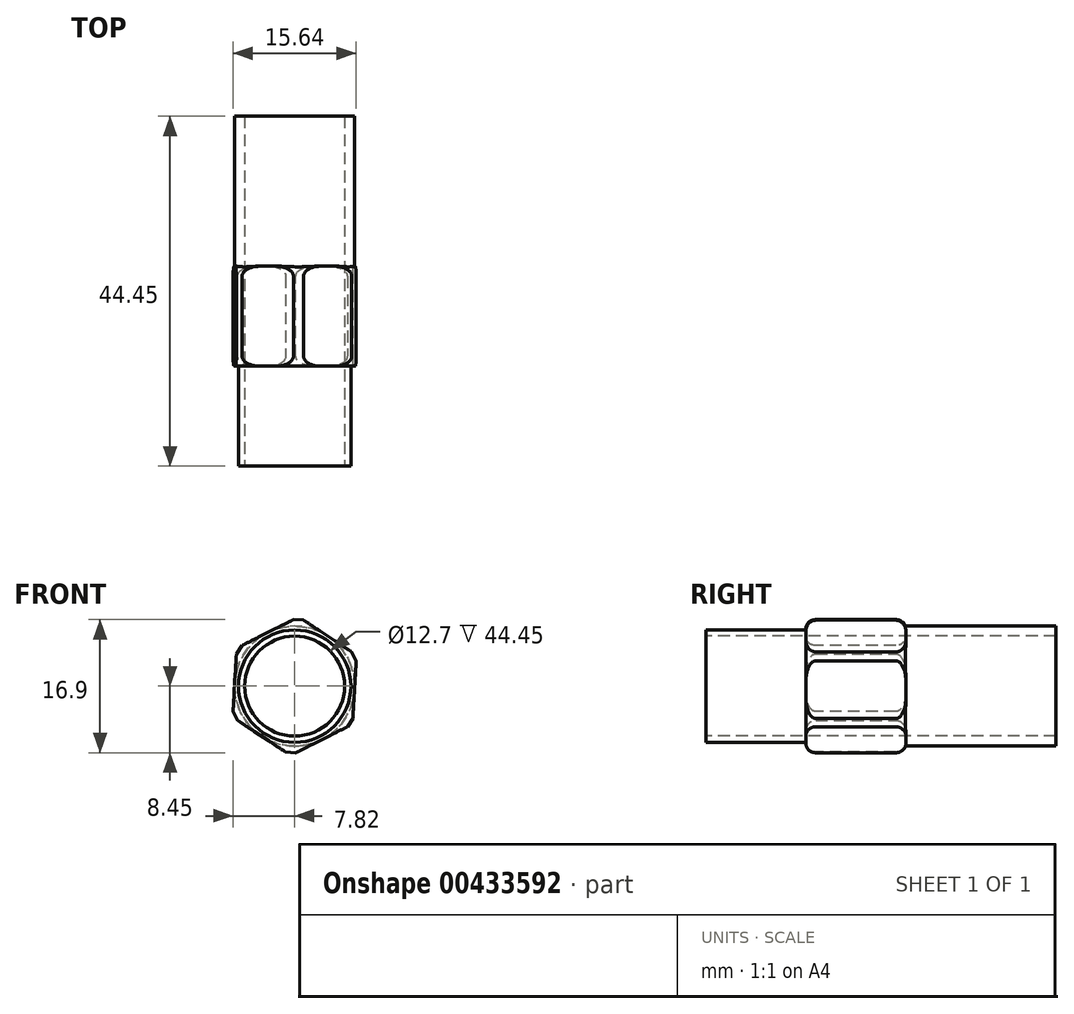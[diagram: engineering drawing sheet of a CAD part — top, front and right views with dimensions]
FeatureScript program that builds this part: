
annotation { "Feature Type Name" : "Feature", "Feature Type Description" : "" }
export const myFeature = defineFeature(function(context is Context, id is Id, definition is map)
    precondition{}
    {
        {
            var Q0;
            Q0=qCreatedBy(makeId("Front.planeOp"),FACE);
            var sketch = newSketch(context, id + "F0", { "sketchPlane" : qUnion([Q0])});
            skCircle(sketch, "E0", {"center": v(0, 0) * mm, "radius": 7.62 * mm});
            skSolve(sketch);
        }
        {
            var Q0;
            Q0=makeQuery(id+"F0.imprint","IMPRINT",FACE,{"disambiguationData":[TD([[makeQuery(id+"F0.imprint","IMPRINT",EDGE,{"derivedFrom":sQuery(id+"F0.wireOp",EDGE,"E0")}),1.0]])]});
            extrude(context, id + "F1", {"entities" : qUnion([Q0]), "depth" : 19.05 * mm});
        }
        {
            var Q0;
            Q0=makeQuery(id+"F1.opExtrude","CAP_FACE",FACE,{"disambiguationData":[OSD([sQuery(id+"F0.wireOp",EDGE,"E0")])],"isStart":false});
            var sketch = newSketch(context, id + "F2", { "sketchPlane" : qUnion([Q0])});
            skCircle(sketch, "E1.cCircle", {"center": v(0, 0) * mm, "radius": 7.62 * mm, "construction": true});
            skLineSegment(sketch, "E1.0", {"start": v(-7.35, 4.84) * mm, "end": v(0.51, 8.78) * mm});
            skLineSegment(sketch, "E1.1", {"start": v(0.51, 8.78) * mm, "end": v(7.86, 3.95) * mm});
            skLineSegment(sketch, "E1.2", {"start": v(7.86, 3.95) * mm, "end": v(7.35, -4.84) * mm});
            skLineSegment(sketch, "E1.3", {"start": v(7.35, -4.84) * mm, "end": v(-0.51, -8.78) * mm});
            skLineSegment(sketch, "E1.4", {"start": v(-0.51, -8.78) * mm, "end": v(-7.86, -3.95) * mm});
            skLineSegment(sketch, "E1.5", {"start": v(-7.86, -3.95) * mm, "end": v(-7.35, 4.84) * mm});
            skPoint(sketch, "E1.0.midPoint", {"position": v(-3.42, 6.8) * mm});
            skSolve(sketch);
        }
        {
            var Q0;
            {var subQ0=sQuery(id+"F2.wireOp",EDGE,"E1.2");var subQ1=sQuery(id+"F2.wireOp",EDGE,"E1.1");var subQ2=makeQuery(id+"F2.imprint","INTERSECT",VERTEX,{"derivedFrom":[subQ1,subQ0]});Q0=makeQuery(id+"F2.imprint","IMPRINT",FACE,{"disambiguationData":[TD([[makeQuery(id+"F2.imprint","IMPRINT",EDGE,{"disambiguationData":[TD([[subQ2,1.0]])],"derivedFrom":subQ1}),-1.0]])]});}
            var Q1;
            {var subQ0=makeQuery(id+"F1.opExtrude","CAP_EDGE",EDGE,{"disambiguationData":[OSD([sQuery(id+"F0.wireOp",EDGE,"E0")])],"isStart":false});var subQ4=makeQuery(id+"F2.imprint","INTERSECT",VERTEX,{"derivedFrom":[subQ0,sQuery(id+"F2.wireOp",EDGE,"E1.0")]});Q1=makeQuery(id+"F2.imprint","IMPRINT",FACE,{"disambiguationData":[TD([[makeQuery(id+"F2.imprint","IMPRINT",EDGE,{"disambiguationData":[TD([[subQ4,1.0]])],"derivedFrom":subQ0}),1.0]])]});}
            var Q2;
            {var subQ0=sQuery(id+"F2.wireOp",EDGE,"E1.3");var subQ1=sQuery(id+"F2.wireOp",EDGE,"E1.2");var subQ2=makeQuery(id+"F2.imprint","INTERSECT",VERTEX,{"derivedFrom":[subQ1,subQ0]});Q2=makeQuery(id+"F2.imprint","IMPRINT",FACE,{"disambiguationData":[TD([[makeQuery(id+"F2.imprint","IMPRINT",EDGE,{"disambiguationData":[TD([[subQ2,1.0]])],"derivedFrom":subQ1}),-1.0]])]});}
            var Q3;
            {var subQ0=sQuery(id+"F2.wireOp",EDGE,"E1.4");var subQ1=sQuery(id+"F2.wireOp",EDGE,"E1.3");var subQ2=makeQuery(id+"F2.imprint","INTERSECT",VERTEX,{"derivedFrom":[subQ1,subQ0]});Q3=makeQuery(id+"F2.imprint","IMPRINT",FACE,{"disambiguationData":[TD([[makeQuery(id+"F2.imprint","IMPRINT",EDGE,{"disambiguationData":[TD([[subQ2,1.0]])],"derivedFrom":subQ1}),-1.0]])]});}
            var Q4;
            {var subQ0=sQuery(id+"F2.wireOp",EDGE,"E1.5");var subQ1=sQuery(id+"F2.wireOp",EDGE,"E1.4");var subQ2=makeQuery(id+"F2.imprint","INTERSECT",VERTEX,{"derivedFrom":[subQ1,subQ0]});Q4=makeQuery(id+"F2.imprint","IMPRINT",FACE,{"disambiguationData":[TD([[makeQuery(id+"F2.imprint","IMPRINT",EDGE,{"disambiguationData":[TD([[subQ2,1.0]])],"derivedFrom":subQ1}),-1.0]])]});}
            var Q5;
            {var subQ0=sQuery(id+"F2.wireOp",EDGE,"E1.5");var subQ1=sQuery(id+"F2.wireOp",EDGE,"E1.0");var subQ2=makeQuery(id+"F2.imprint","INTERSECT",VERTEX,{"derivedFrom":[subQ1,subQ0]});Q5=makeQuery(id+"F2.imprint","IMPRINT",FACE,{"disambiguationData":[TD([[makeQuery(id+"F2.imprint","IMPRINT",EDGE,{"disambiguationData":[TD([[subQ2,-1.0]])],"derivedFrom":subQ1}),-1.0]])]});}
            var Q6;
            {var subQ0=sQuery(id+"F2.wireOp",EDGE,"E1.1");var subQ1=sQuery(id+"F2.wireOp",EDGE,"E1.0");var subQ2=makeQuery(id+"F2.imprint","INTERSECT",VERTEX,{"derivedFrom":[subQ1,subQ0]});Q6=makeQuery(id+"F2.imprint","IMPRINT",FACE,{"disambiguationData":[TD([[makeQuery(id+"F2.imprint","IMPRINT",EDGE,{"disambiguationData":[TD([[subQ2,1.0]])],"derivedFrom":subQ1}),-1.0]])]});}
            extrude(context, id + "F3", {"entities" : qUnion([Q0, Q1, Q2, Q3, Q4, Q5, Q6]), "operationType" : NewBodyOperationType.ADD, "depth" : 12.7 * mm});
        }
        {
            var Q0;
            Q0=makeQuery(id+"F3.opExtrude","SWEPT_EDGE",EDGE,{"disambiguationData":[OSD([sQuery(id+"F2.wireOp",EDGE,"E1.1"),sQuery(id+"F2.wireOp",EDGE,"E1.2")])]});
            var Q1;
            Q1=makeQuery(id+"F3.opExtrude","SWEPT_EDGE",EDGE,{"disambiguationData":[OSD([sQuery(id+"F2.wireOp",EDGE,"E1.2"),sQuery(id+"F2.wireOp",EDGE,"E1.3")])]});
            var Q2;
            Q2=makeQuery(id+"F3.opExtrude","SWEPT_EDGE",EDGE,{"disambiguationData":[OSD([sQuery(id+"F2.wireOp",EDGE,"E1.3"),sQuery(id+"F2.wireOp",EDGE,"E1.4")])]});
            var Q3;
            Q3=makeQuery(id+"F3.opExtrude","SWEPT_EDGE",EDGE,{"disambiguationData":[OSD([sQuery(id+"F2.wireOp",EDGE,"E1.4"),sQuery(id+"F2.wireOp",EDGE,"E1.5")])]});
            var Q4;
            Q4=makeQuery(id+"F3.opExtrude","SWEPT_EDGE",EDGE,{"disambiguationData":[OSD([sQuery(id+"F2.wireOp",EDGE,"E1.0"),sQuery(id+"F2.wireOp",EDGE,"E1.5")])]});
            var Q5;
            Q5=makeQuery(id+"F3.opExtrude","SWEPT_EDGE",EDGE,{"disambiguationData":[OSD([sQuery(id+"F2.wireOp",EDGE,"E1.0"),sQuery(id+"F2.wireOp",EDGE,"E1.1")])]});
            chamfer(context, id + "F4", {"entities" : qUnion([Q0, Q1, Q2, Q3, Q4, Q5]), "width" : 1.27 * mm, "tangentPropagation" : true});
        }
        {
            var Q0;
            {var subQ0=sQuery(id+"F2.wireOp",EDGE,"E1.0");var subQ1=sQuery(id+"F2.wireOp",EDGE,"E1.1");var subQ2=makeQuery(id+"F3.opExtrude","CAP_FACE",FACE,{"disambiguationData":[OSD([subQ0,subQ1,sQuery(id+"F2.wireOp",EDGE,"E1.2"),sQuery(id+"F2.wireOp",EDGE,"E1.3"),sQuery(id+"F2.wireOp",EDGE,"E1.4"),sQuery(id+"F2.wireOp",EDGE,"E1.5")])],"isStart":true});Q0=makeQuery(id+"F4.opChamfer","BLEND_EDGE",EDGE,{"blendedFrom":[makeQuery(id+"F3.opExtrude","SWEPT_EDGE",EDGE,{"disambiguationData":[OSD([subQ0,subQ1])]}),makeQuery(id+"F3.boolean.opBoolean","SPLIT",FACE,{"disambiguationData":[TD([makeQuery(id+"F1.opExtrude","SWEPT_FACE",FACE,{"disambiguationData":[OSD([sQuery(id+"F0.wireOp",EDGE,"E0")])]}),makeQuery(id+"F3.opExtrude","SWEPT_FACE",FACE,{"disambiguationData":[OSD([subQ0])]}),subQ2,makeQuery(id+"F3.opExtrude","SWEPT_FACE",FACE,{"disambiguationData":[OSD([subQ1])]})])],"derivedFrom":subQ2})],"blendedInto":[makeQuery(id+"F3.boolean.opBoolean","SPLIT",FACE,{"disambiguationData":[TD([makeQuery(id+"F1.opExtrude","SWEPT_FACE",FACE,{"disambiguationData":[OSD([sQuery(id+"F0.wireOp",EDGE,"E0")])]}),makeQuery(id+"F3.opExtrude","SWEPT_FACE",FACE,{"disambiguationData":[OSD([subQ0])]}),subQ2,makeQuery(id+"F3.opExtrude","SWEPT_FACE",FACE,{"disambiguationData":[OSD([subQ1])]})])],"derivedFrom":subQ2})]});}
            var Q1;
            {var subQ0=sQuery(id+"F2.wireOp",EDGE,"E1.5");var subQ1=sQuery(id+"F2.wireOp",EDGE,"E1.0");var subQ2=makeQuery(id+"F3.opExtrude","CAP_FACE",FACE,{"disambiguationData":[OSD([subQ1,sQuery(id+"F2.wireOp",EDGE,"E1.1"),sQuery(id+"F2.wireOp",EDGE,"E1.2"),sQuery(id+"F2.wireOp",EDGE,"E1.3"),sQuery(id+"F2.wireOp",EDGE,"E1.4"),subQ0])],"isStart":true});Q1=makeQuery(id+"F4.opChamfer","BLEND_EDGE",EDGE,{"blendedFrom":[makeQuery(id+"F3.opExtrude","SWEPT_EDGE",EDGE,{"disambiguationData":[OSD([subQ1,subQ0])]}),makeQuery(id+"F3.boolean.opBoolean","SPLIT",FACE,{"disambiguationData":[TD([makeQuery(id+"F1.opExtrude","SWEPT_FACE",FACE,{"disambiguationData":[OSD([sQuery(id+"F0.wireOp",EDGE,"E0")])]}),makeQuery(id+"F3.opExtrude","SWEPT_FACE",FACE,{"disambiguationData":[OSD([subQ1])]}),subQ2,makeQuery(id+"F3.opExtrude","SWEPT_FACE",FACE,{"disambiguationData":[OSD([subQ0])]})])],"derivedFrom":subQ2})],"blendedInto":[makeQuery(id+"F3.boolean.opBoolean","SPLIT",FACE,{"disambiguationData":[TD([makeQuery(id+"F1.opExtrude","SWEPT_FACE",FACE,{"disambiguationData":[OSD([sQuery(id+"F0.wireOp",EDGE,"E0")])]}),makeQuery(id+"F3.opExtrude","SWEPT_FACE",FACE,{"disambiguationData":[OSD([subQ1])]}),subQ2,makeQuery(id+"F3.opExtrude","SWEPT_FACE",FACE,{"disambiguationData":[OSD([subQ0])]})])],"derivedFrom":subQ2})]});}
            var Q2;
            {var subQ0=sQuery(id+"F2.wireOp",EDGE,"E1.5");var subQ1=sQuery(id+"F2.wireOp",EDGE,"E1.4");var subQ2=makeQuery(id+"F3.opExtrude","CAP_FACE",FACE,{"disambiguationData":[OSD([sQuery(id+"F2.wireOp",EDGE,"E1.0"),sQuery(id+"F2.wireOp",EDGE,"E1.1"),sQuery(id+"F2.wireOp",EDGE,"E1.2"),sQuery(id+"F2.wireOp",EDGE,"E1.3"),subQ1,subQ0])],"isStart":true});Q2=makeQuery(id+"F4.opChamfer","BLEND_EDGE",EDGE,{"blendedFrom":[makeQuery(id+"F3.opExtrude","SWEPT_EDGE",EDGE,{"disambiguationData":[OSD([subQ1,subQ0])]}),makeQuery(id+"F3.boolean.opBoolean","SPLIT",FACE,{"disambiguationData":[TD([makeQuery(id+"F1.opExtrude","SWEPT_FACE",FACE,{"disambiguationData":[OSD([sQuery(id+"F0.wireOp",EDGE,"E0")])]}),subQ2,makeQuery(id+"F3.opExtrude","SWEPT_FACE",FACE,{"disambiguationData":[OSD([subQ1])]}),makeQuery(id+"F3.opExtrude","SWEPT_FACE",FACE,{"disambiguationData":[OSD([subQ0])]})])],"derivedFrom":subQ2})],"blendedInto":[makeQuery(id+"F3.boolean.opBoolean","SPLIT",FACE,{"disambiguationData":[TD([makeQuery(id+"F1.opExtrude","SWEPT_FACE",FACE,{"disambiguationData":[OSD([sQuery(id+"F0.wireOp",EDGE,"E0")])]}),subQ2,makeQuery(id+"F3.opExtrude","SWEPT_FACE",FACE,{"disambiguationData":[OSD([subQ1])]}),makeQuery(id+"F3.opExtrude","SWEPT_FACE",FACE,{"disambiguationData":[OSD([subQ0])]})])],"derivedFrom":subQ2})]});}
            var Q3;
            {var subQ0=sQuery(id+"F2.wireOp",EDGE,"E1.4");var subQ1=sQuery(id+"F2.wireOp",EDGE,"E1.3");var subQ2=makeQuery(id+"F3.opExtrude","CAP_FACE",FACE,{"disambiguationData":[OSD([sQuery(id+"F2.wireOp",EDGE,"E1.0"),sQuery(id+"F2.wireOp",EDGE,"E1.1"),sQuery(id+"F2.wireOp",EDGE,"E1.2"),subQ1,subQ0,sQuery(id+"F2.wireOp",EDGE,"E1.5")])],"isStart":true});Q3=makeQuery(id+"F4.opChamfer","BLEND_EDGE",EDGE,{"blendedFrom":[makeQuery(id+"F3.opExtrude","SWEPT_EDGE",EDGE,{"disambiguationData":[OSD([subQ1,subQ0])]}),makeQuery(id+"F3.boolean.opBoolean","SPLIT",FACE,{"disambiguationData":[TD([makeQuery(id+"F1.opExtrude","SWEPT_FACE",FACE,{"disambiguationData":[OSD([sQuery(id+"F0.wireOp",EDGE,"E0")])]}),subQ2,makeQuery(id+"F3.opExtrude","SWEPT_FACE",FACE,{"disambiguationData":[OSD([subQ1])]}),makeQuery(id+"F3.opExtrude","SWEPT_FACE",FACE,{"disambiguationData":[OSD([subQ0])]})])],"derivedFrom":subQ2})],"blendedInto":[makeQuery(id+"F3.boolean.opBoolean","SPLIT",FACE,{"disambiguationData":[TD([makeQuery(id+"F1.opExtrude","SWEPT_FACE",FACE,{"disambiguationData":[OSD([sQuery(id+"F0.wireOp",EDGE,"E0")])]}),subQ2,makeQuery(id+"F3.opExtrude","SWEPT_FACE",FACE,{"disambiguationData":[OSD([subQ1])]}),makeQuery(id+"F3.opExtrude","SWEPT_FACE",FACE,{"disambiguationData":[OSD([subQ0])]})])],"derivedFrom":subQ2})]});}
            var Q4;
            {var subQ0=sQuery(id+"F2.wireOp",EDGE,"E1.3");var subQ1=sQuery(id+"F2.wireOp",EDGE,"E1.2");var subQ2=makeQuery(id+"F3.opExtrude","CAP_FACE",FACE,{"disambiguationData":[OSD([sQuery(id+"F2.wireOp",EDGE,"E1.0"),sQuery(id+"F2.wireOp",EDGE,"E1.1"),subQ1,subQ0,sQuery(id+"F2.wireOp",EDGE,"E1.4"),sQuery(id+"F2.wireOp",EDGE,"E1.5")])],"isStart":true});Q4=makeQuery(id+"F4.opChamfer","BLEND_EDGE",EDGE,{"blendedFrom":[makeQuery(id+"F3.opExtrude","SWEPT_EDGE",EDGE,{"disambiguationData":[OSD([subQ1,subQ0])]}),makeQuery(id+"F3.boolean.opBoolean","SPLIT",FACE,{"disambiguationData":[TD([makeQuery(id+"F1.opExtrude","SWEPT_FACE",FACE,{"disambiguationData":[OSD([sQuery(id+"F0.wireOp",EDGE,"E0")])]}),subQ2,makeQuery(id+"F3.opExtrude","SWEPT_FACE",FACE,{"disambiguationData":[OSD([subQ1])]}),makeQuery(id+"F3.opExtrude","SWEPT_FACE",FACE,{"disambiguationData":[OSD([subQ0])]})])],"derivedFrom":subQ2})],"blendedInto":[makeQuery(id+"F3.boolean.opBoolean","SPLIT",FACE,{"disambiguationData":[TD([makeQuery(id+"F1.opExtrude","SWEPT_FACE",FACE,{"disambiguationData":[OSD([sQuery(id+"F0.wireOp",EDGE,"E0")])]}),subQ2,makeQuery(id+"F3.opExtrude","SWEPT_FACE",FACE,{"disambiguationData":[OSD([subQ1])]}),makeQuery(id+"F3.opExtrude","SWEPT_FACE",FACE,{"disambiguationData":[OSD([subQ0])]})])],"derivedFrom":subQ2})]});}
            var Q5;
            {var subQ0=sQuery(id+"F2.wireOp",EDGE,"E1.2");var subQ1=sQuery(id+"F2.wireOp",EDGE,"E1.1");var subQ2=makeQuery(id+"F3.opExtrude","CAP_FACE",FACE,{"disambiguationData":[OSD([sQuery(id+"F2.wireOp",EDGE,"E1.0"),subQ1,subQ0,sQuery(id+"F2.wireOp",EDGE,"E1.3"),sQuery(id+"F2.wireOp",EDGE,"E1.4"),sQuery(id+"F2.wireOp",EDGE,"E1.5")])],"isStart":true});Q5=makeQuery(id+"F4.opChamfer","BLEND_EDGE",EDGE,{"blendedFrom":[makeQuery(id+"F3.opExtrude","SWEPT_EDGE",EDGE,{"disambiguationData":[OSD([subQ1,subQ0])]}),makeQuery(id+"F3.boolean.opBoolean","SPLIT",FACE,{"disambiguationData":[TD([makeQuery(id+"F1.opExtrude","SWEPT_FACE",FACE,{"disambiguationData":[OSD([sQuery(id+"F0.wireOp",EDGE,"E0")])]}),subQ2,makeQuery(id+"F3.opExtrude","SWEPT_FACE",FACE,{"disambiguationData":[OSD([subQ1])]}),makeQuery(id+"F3.opExtrude","SWEPT_FACE",FACE,{"disambiguationData":[OSD([subQ0])]})])],"derivedFrom":subQ2})],"blendedInto":[makeQuery(id+"F3.boolean.opBoolean","SPLIT",FACE,{"disambiguationData":[TD([makeQuery(id+"F1.opExtrude","SWEPT_FACE",FACE,{"disambiguationData":[OSD([sQuery(id+"F0.wireOp",EDGE,"E0")])]}),subQ2,makeQuery(id+"F3.opExtrude","SWEPT_FACE",FACE,{"disambiguationData":[OSD([subQ1])]}),makeQuery(id+"F3.opExtrude","SWEPT_FACE",FACE,{"disambiguationData":[OSD([subQ0])]})])],"derivedFrom":subQ2})]});}
            var Q6;
            {var subQ0=sQuery(id+"F2.wireOp",EDGE,"E1.2");var subQ1=sQuery(id+"F2.wireOp",EDGE,"E1.1");Q6=makeQuery(id+"F4.opChamfer","BLEND_EDGE",EDGE,{"blendedFrom":[makeQuery(id+"F3.opExtrude","SWEPT_EDGE",EDGE,{"disambiguationData":[OSD([subQ1,subQ0])]}),makeQuery(id+"F3.opExtrude","CAP_FACE",FACE,{"disambiguationData":[OSD([sQuery(id+"F2.wireOp",EDGE,"E1.0"),subQ1,subQ0,sQuery(id+"F2.wireOp",EDGE,"E1.3"),sQuery(id+"F2.wireOp",EDGE,"E1.4"),sQuery(id+"F2.wireOp",EDGE,"E1.5")])],"isStart":false})],"blendedInto":[makeQuery(id+"F3.opExtrude","CAP_FACE",FACE,{"disambiguationData":[OSD([sQuery(id+"F2.wireOp",EDGE,"E1.0"),subQ1,subQ0,sQuery(id+"F2.wireOp",EDGE,"E1.3"),sQuery(id+"F2.wireOp",EDGE,"E1.4"),sQuery(id+"F2.wireOp",EDGE,"E1.5")])],"isStart":false})]});}
            var Q7;
            {var subQ0=sQuery(id+"F2.wireOp",EDGE,"E1.1");var subQ1=sQuery(id+"F2.wireOp",EDGE,"E1.0");Q7=makeQuery(id+"F4.opChamfer","BLEND_EDGE",EDGE,{"blendedFrom":[makeQuery(id+"F3.opExtrude","SWEPT_EDGE",EDGE,{"disambiguationData":[OSD([subQ1,subQ0])]}),makeQuery(id+"F3.opExtrude","CAP_FACE",FACE,{"disambiguationData":[OSD([subQ1,subQ0,sQuery(id+"F2.wireOp",EDGE,"E1.2"),sQuery(id+"F2.wireOp",EDGE,"E1.3"),sQuery(id+"F2.wireOp",EDGE,"E1.4"),sQuery(id+"F2.wireOp",EDGE,"E1.5")])],"isStart":false})],"blendedInto":[makeQuery(id+"F3.opExtrude","CAP_FACE",FACE,{"disambiguationData":[OSD([subQ1,subQ0,sQuery(id+"F2.wireOp",EDGE,"E1.2"),sQuery(id+"F2.wireOp",EDGE,"E1.3"),sQuery(id+"F2.wireOp",EDGE,"E1.4"),sQuery(id+"F2.wireOp",EDGE,"E1.5")])],"isStart":false})]});}
            var Q8;
            {var subQ0=sQuery(id+"F2.wireOp",EDGE,"E1.5");var subQ1=sQuery(id+"F2.wireOp",EDGE,"E1.0");Q8=makeQuery(id+"F4.opChamfer","BLEND_EDGE",EDGE,{"blendedFrom":[makeQuery(id+"F3.opExtrude","SWEPT_EDGE",EDGE,{"disambiguationData":[OSD([subQ1,subQ0])]}),makeQuery(id+"F3.opExtrude","CAP_FACE",FACE,{"disambiguationData":[OSD([subQ1,sQuery(id+"F2.wireOp",EDGE,"E1.1"),sQuery(id+"F2.wireOp",EDGE,"E1.2"),sQuery(id+"F2.wireOp",EDGE,"E1.3"),sQuery(id+"F2.wireOp",EDGE,"E1.4"),subQ0])],"isStart":false})],"blendedInto":[makeQuery(id+"F3.opExtrude","CAP_FACE",FACE,{"disambiguationData":[OSD([subQ1,sQuery(id+"F2.wireOp",EDGE,"E1.1"),sQuery(id+"F2.wireOp",EDGE,"E1.2"),sQuery(id+"F2.wireOp",EDGE,"E1.3"),sQuery(id+"F2.wireOp",EDGE,"E1.4"),subQ0])],"isStart":false})]});}
            var Q9;
            {var subQ0=sQuery(id+"F2.wireOp",EDGE,"E1.5");var subQ1=sQuery(id+"F2.wireOp",EDGE,"E1.4");Q9=makeQuery(id+"F4.opChamfer","BLEND_EDGE",EDGE,{"blendedFrom":[makeQuery(id+"F3.opExtrude","SWEPT_EDGE",EDGE,{"disambiguationData":[OSD([subQ1,subQ0])]}),makeQuery(id+"F3.opExtrude","CAP_FACE",FACE,{"disambiguationData":[OSD([sQuery(id+"F2.wireOp",EDGE,"E1.0"),sQuery(id+"F2.wireOp",EDGE,"E1.1"),sQuery(id+"F2.wireOp",EDGE,"E1.2"),sQuery(id+"F2.wireOp",EDGE,"E1.3"),subQ1,subQ0])],"isStart":false})],"blendedInto":[makeQuery(id+"F3.opExtrude","CAP_FACE",FACE,{"disambiguationData":[OSD([sQuery(id+"F2.wireOp",EDGE,"E1.0"),sQuery(id+"F2.wireOp",EDGE,"E1.1"),sQuery(id+"F2.wireOp",EDGE,"E1.2"),sQuery(id+"F2.wireOp",EDGE,"E1.3"),subQ1,subQ0])],"isStart":false})]});}
            var Q10;
            {var subQ0=sQuery(id+"F2.wireOp",EDGE,"E1.4");var subQ1=sQuery(id+"F2.wireOp",EDGE,"E1.3");Q10=makeQuery(id+"F4.opChamfer","BLEND_EDGE",EDGE,{"blendedFrom":[makeQuery(id+"F3.opExtrude","SWEPT_EDGE",EDGE,{"disambiguationData":[OSD([subQ1,subQ0])]}),makeQuery(id+"F3.opExtrude","CAP_FACE",FACE,{"disambiguationData":[OSD([sQuery(id+"F2.wireOp",EDGE,"E1.0"),sQuery(id+"F2.wireOp",EDGE,"E1.1"),sQuery(id+"F2.wireOp",EDGE,"E1.2"),subQ1,subQ0,sQuery(id+"F2.wireOp",EDGE,"E1.5")])],"isStart":false})],"blendedInto":[makeQuery(id+"F3.opExtrude","CAP_FACE",FACE,{"disambiguationData":[OSD([sQuery(id+"F2.wireOp",EDGE,"E1.0"),sQuery(id+"F2.wireOp",EDGE,"E1.1"),sQuery(id+"F2.wireOp",EDGE,"E1.2"),subQ1,subQ0,sQuery(id+"F2.wireOp",EDGE,"E1.5")])],"isStart":false})]});}
            var Q11;
            {var subQ0=sQuery(id+"F2.wireOp",EDGE,"E1.3");var subQ1=sQuery(id+"F2.wireOp",EDGE,"E1.2");Q11=makeQuery(id+"F4.opChamfer","BLEND_EDGE",EDGE,{"blendedFrom":[makeQuery(id+"F3.opExtrude","SWEPT_EDGE",EDGE,{"disambiguationData":[OSD([subQ1,subQ0])]}),makeQuery(id+"F3.opExtrude","CAP_FACE",FACE,{"disambiguationData":[OSD([sQuery(id+"F2.wireOp",EDGE,"E1.0"),sQuery(id+"F2.wireOp",EDGE,"E1.1"),subQ1,subQ0,sQuery(id+"F2.wireOp",EDGE,"E1.4"),sQuery(id+"F2.wireOp",EDGE,"E1.5")])],"isStart":false})],"blendedInto":[makeQuery(id+"F3.opExtrude","CAP_FACE",FACE,{"disambiguationData":[OSD([sQuery(id+"F2.wireOp",EDGE,"E1.0"),sQuery(id+"F2.wireOp",EDGE,"E1.1"),subQ1,subQ0,sQuery(id+"F2.wireOp",EDGE,"E1.4"),sQuery(id+"F2.wireOp",EDGE,"E1.5")])],"isStart":false})]});}
            fillet(context, id + "F5", {"entities" : qUnion([Q0, Q1, Q2, Q3, Q4, Q5, Q6, Q7, Q8, Q9, Q10, Q11]), "radius" : 1.27 * mm, "tangentPropagation" : true, "allowEdgeOverflow" : false});
        }
        {
            var Q0;
            Q0=makeQuery(id+"F3.opExtrude","CAP_FACE",FACE,{"disambiguationData":[OSD([sQuery(id+"F2.wireOp",EDGE,"E1.0"),sQuery(id+"F2.wireOp",EDGE,"E1.1"),sQuery(id+"F2.wireOp",EDGE,"E1.2"),sQuery(id+"F2.wireOp",EDGE,"E1.3"),sQuery(id+"F2.wireOp",EDGE,"E1.4"),sQuery(id+"F2.wireOp",EDGE,"E1.5")])],"isStart":false});
            var sketch = newSketch(context, id + "F6", { "sketchPlane" : qUnion([Q0])});
            skCircle(sketch, "E2", {"center": v(0, 0) * mm, "radius": 7.14 * mm});
            skSolve(sketch);
        }
        {
            var Q0;
            Q0=qSketchRegion(id+"F6",true);
            extrude(context, id + "F7", {"entities" : qUnion([Q0]), "operationType" : NewBodyOperationType.ADD, "depth" : 12.7 * mm});
        }
        {
            var Q0;
            Q0=makeQuery(id+"F7.opExtrude","CAP_FACE",FACE,{"disambiguationData":[OSD([sQuery(id+"F6.wireOp",EDGE,"E2")])],"isStart":false});
            var sketch = newSketch(context, id + "F8", { "sketchPlane" : qUnion([Q0])});
            skCircle(sketch, "E3", {"center": v(0, 0) * mm, "radius": 6.35 * mm});
            skSolve(sketch);
        }
        {
            var Q0;
            Q0=makeQuery(id+"F8.imprint","IMPRINT",FACE,{"disambiguationData":[TD([[makeQuery(id+"F8.imprint","IMPRINT",EDGE,{"derivedFrom":sQuery(id+"F8.wireOp",EDGE,"E3")}),1.0]])]});
            extrude(context, id + "F9", {"entities" : qUnion([Q0]), "operationType" : NewBodyOperationType.REMOVE, "endBound" : BoundingType.THROUGH_ALL, "oppositeDirection" : true, "depth" : 25.4 * mm});
        }
    });
